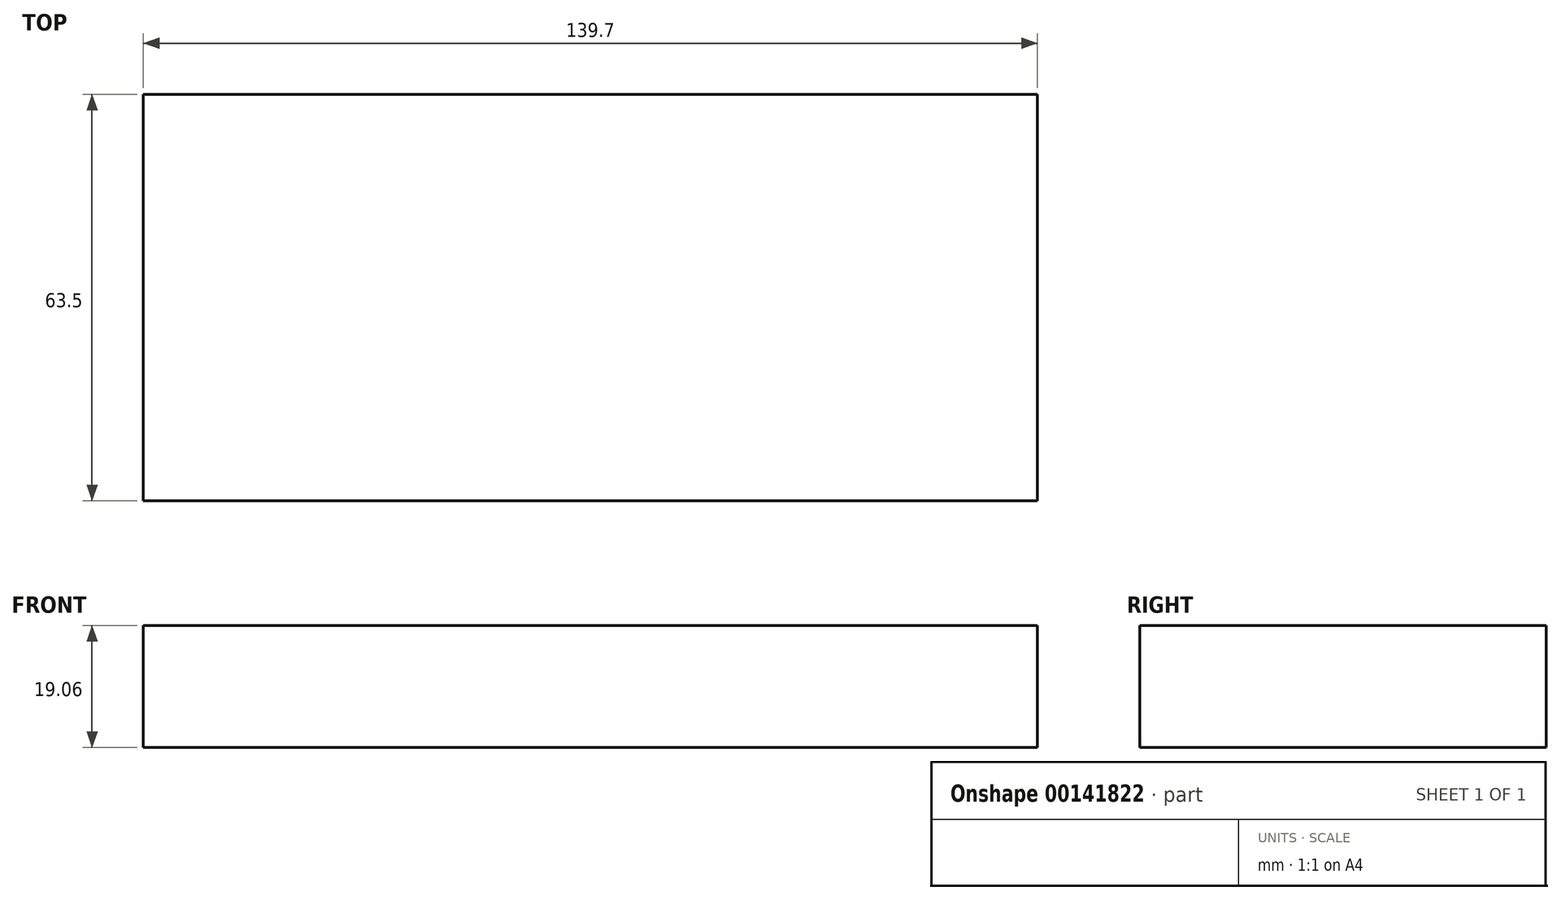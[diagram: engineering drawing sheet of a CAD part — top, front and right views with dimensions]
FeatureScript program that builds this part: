
annotation { "Feature Type Name" : "Feature", "Feature Type Description" : "" }
export const myFeature = defineFeature(function(context is Context, id is Id, definition is map)
    precondition{}
    {
        {
            var Q0;
            Q0=qCreatedBy(makeId("Top.planeOp"),FACE);
            var sketch = newSketch(context, id + "F0", { "sketchPlane" : qUnion([Q0])});
            skLineSegment(sketch, "E0.bottom", {"start": v(-69.85, -31.75) * mm, "end": v(69.85, -31.75) * mm});
            skLineSegment(sketch, "E0.top", {"start": v(-69.85, 31.75) * mm, "end": v(69.85, 31.75) * mm});
            skLineSegment(sketch, "E0.left", {"start": v(-69.85, -31.75) * mm, "end": v(-69.85, 31.75) * mm});
            skLineSegment(sketch, "E0.right", {"start": v(69.85, -31.75) * mm, "end": v(69.85, 31.75) * mm});
            skLineSegment(sketch, "E1", {"start": v(-69.85, -31.75) * mm, "end": v(69.85, 31.75) * mm});
            skSolve(sketch);
        }
        {
            var Q0;
            Q0 = qSketchRegion(id + "F0", true);
            extrude(context, id + "F1", {"entities" : qUnion([Q0]), "endBound" : BoundingType.SYMMETRIC, "depth" : 19.05 * mm});
        }
    });
